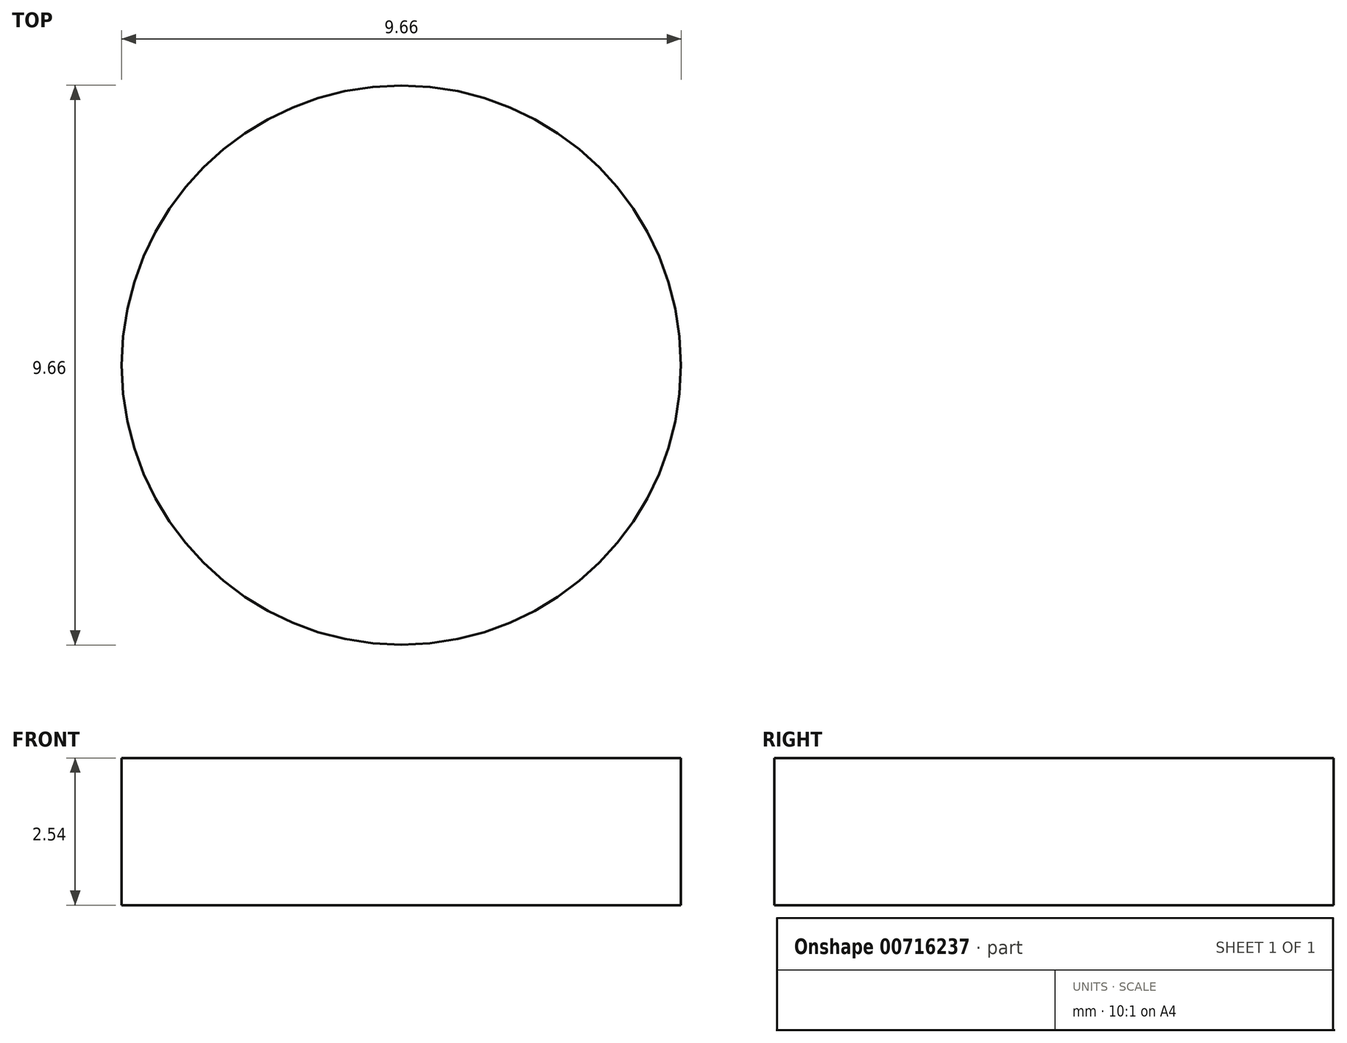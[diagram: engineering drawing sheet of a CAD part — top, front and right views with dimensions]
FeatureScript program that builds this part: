
annotation { "Feature Type Name" : "Feature", "Feature Type Description" : "" }
export const myFeature = defineFeature(function(context is Context, id is Id, definition is map)
    precondition{}
    {
        {
            var Q0;
            Q0=qCreatedBy(makeId("Top.planeOp"),FACE);
            var sketch = newSketch(context, id + "F0", { "sketchPlane" : qUnion([Q0])});
            skCircle(sketch, "E0", {"center": v(0, 0) * mm, "radius": 4.83 * mm});
            skSolve(sketch);
        }
        {
            var Q0;
            Q0=makeQuery(id+"F0.imprint","IMPRINT",FACE,{"disambiguationData":[TD([[makeQuery(id+"F0.imprint","IMPRINT",EDGE,{"derivedFrom":sQuery(id+"F0.wireOp",EDGE,"E0")}),1.0]])]});
            extrude(context, id + "F1", {"entities" : qUnion([Q0]), "depth" : 2.54 * mm, "offsetDistance" : 25.4 * mm});
        }
    });
